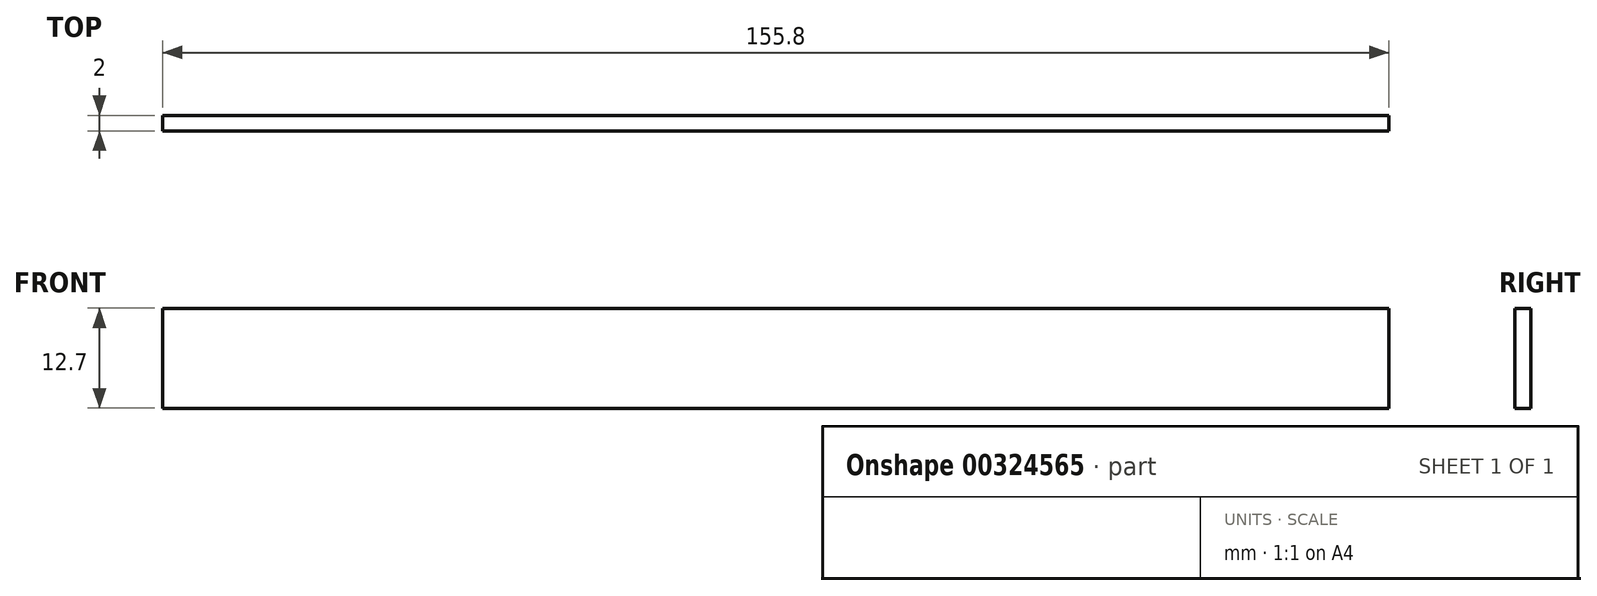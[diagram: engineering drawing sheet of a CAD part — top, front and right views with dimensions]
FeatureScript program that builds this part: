
annotation { "Feature Type Name" : "Feature", "Feature Type Description" : "" }
export const myFeature = defineFeature(function(context is Context, id is Id, definition is map)
    precondition{}
    {
        {
            var Q0;
            Q0=qCreatedBy(makeId("Front.planeOp"),FACE);
            var sketch = newSketch(context, id + "F0", { "sketchPlane" : qUnion([Q0])});
            skLineSegment(sketch, "E0.bottom", {"start": v(-85.03, 16.88) * mm, "end": v(70.77, 16.88) * mm});
            skLineSegment(sketch, "E0.top", {"start": v(-85.03, 4.18) * mm, "end": v(70.77, 4.18) * mm});
            skLineSegment(sketch, "E0.left", {"start": v(-85.03, 16.88) * mm, "end": v(-85.03, 4.18) * mm});
            skLineSegment(sketch, "E0.right", {"start": v(70.77, 16.88) * mm, "end": v(70.77, 4.18) * mm});
            skSolve(sketch);
        }
        {
            var Q0;
            Q0=makeQuery(id+"F0.imprint","IMPRINT",FACE,{"disambiguationData":[TD([[makeQuery(id+"F0.imprint","IMPRINT",EDGE,{"derivedFrom":sQuery(id+"F0.wireOp",EDGE,"E0.bottom")}),-1.0]])]});
            extrude(context, id + "F1", {"entities" : qUnion([Q0]), "depth" : 2 * mm});
        }
    });
